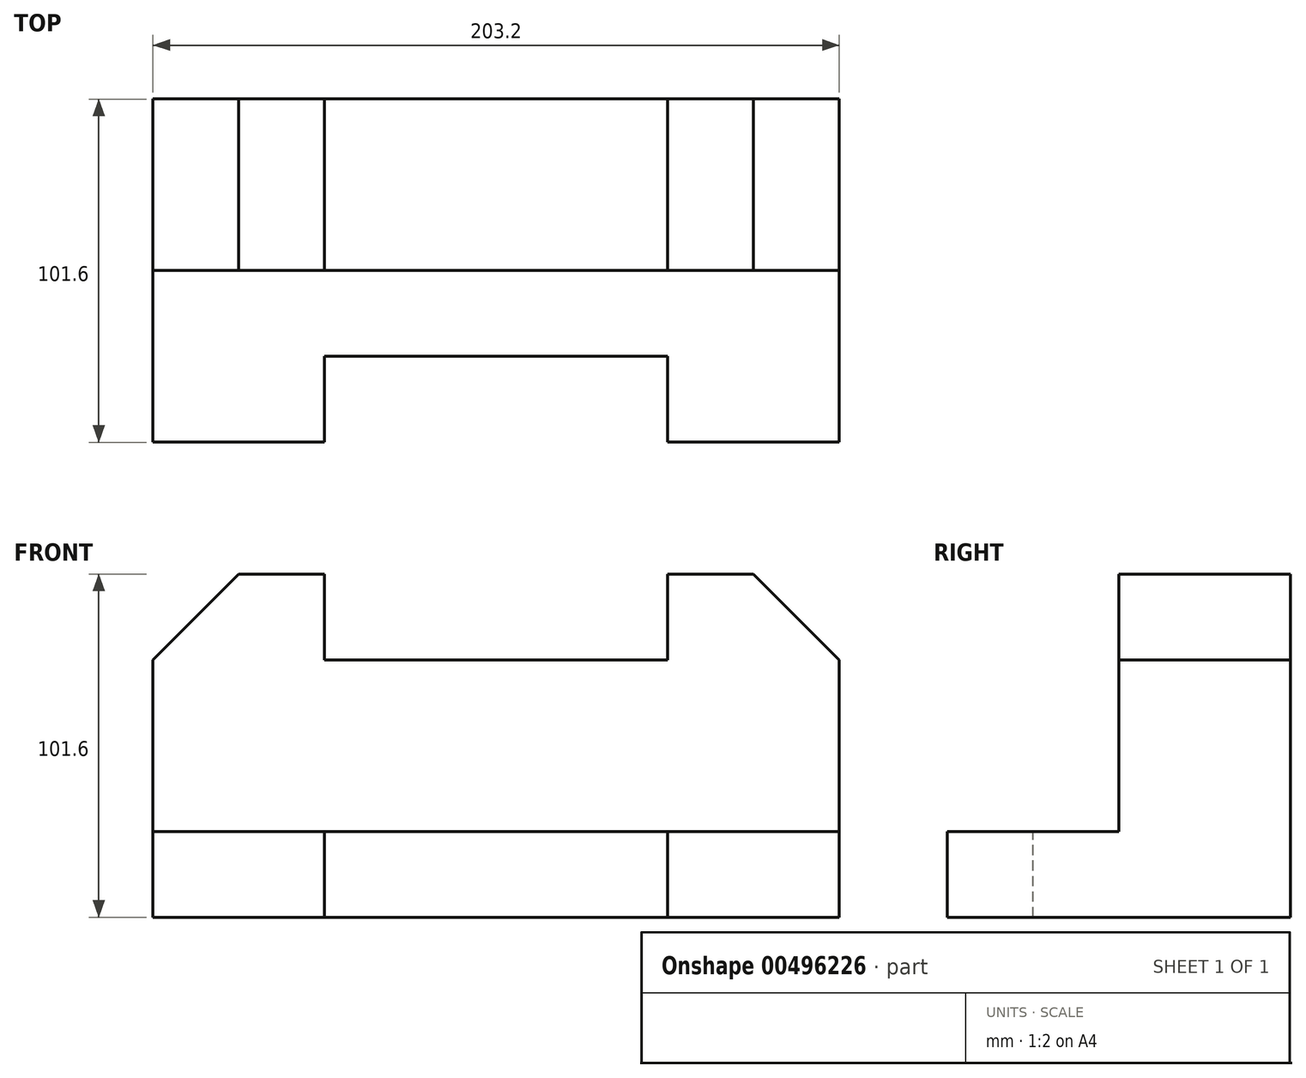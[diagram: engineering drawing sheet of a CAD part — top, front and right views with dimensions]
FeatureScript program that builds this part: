
annotation { "Feature Type Name" : "Feature", "Feature Type Description" : "" }
export const myFeature = defineFeature(function(context is Context, id is Id, definition is map)
    precondition{}
    {
        {
            var Q0;
            Q0=qCreatedBy(makeId("Top.planeOp"),FACE);
            var sketch = newSketch(context, id + "F0", { "sketchPlane" : qUnion([Q0])});
            skLineSegment(sketch, "E0.bottom", {"start": v(-130.96, 84.04) * mm, "end": v(72.24, 84.04) * mm});
            skLineSegment(sketch, "E0.top", {"start": v(-130.96, -17.56) * mm, "end": v(72.24, -17.56) * mm});
            skLineSegment(sketch, "E0.left", {"start": v(-130.96, 84.04) * mm, "end": v(-130.96, -17.56) * mm});
            skLineSegment(sketch, "E0.right", {"start": v(72.24, 84.04) * mm, "end": v(72.24, -17.56) * mm});
            skSolve(sketch);
        }
        {
            var Q0;
            Q0 = qSketchRegion(id + "F0", true);
            extrude(context, id + "F1", {"entities" : qUnion([Q0]), "depth" : 25.4 * mm});
        }
        {
            var Q0;
            Q0=makeQuery(id+"F1.opExtrude","CAP_FACE",FACE,{"disambiguationData":[OSD([sQuery(id+"F0.wireOp",EDGE,"E0.bottom"),sQuery(id+"F0.wireOp",EDGE,"E0.top"),sQuery(id+"F0.wireOp",EDGE,"E0.left"),sQuery(id+"F0.wireOp",EDGE,"E0.right")])],"isStart":false});
            var sketch = newSketch(context, id + "F2", { "sketchPlane" : qUnion([Q0])});
            skLineSegment(sketch, "E1.bottom", {"start": v(-130.96, 84.04) * mm, "end": v(72.24, 84.04) * mm});
            skLineSegment(sketch, "E1.top", {"start": v(-130.96, 33.24) * mm, "end": v(72.24, 33.24) * mm});
            skLineSegment(sketch, "E1.left", {"start": v(-130.96, 84.04) * mm, "end": v(-130.96, 33.24) * mm});
            skLineSegment(sketch, "E1.right", {"start": v(72.24, 84.04) * mm, "end": v(72.24, 33.24) * mm});
            skSolve(sketch);
        }
        {
            var Q0;
            Q0=makeQuery(id+"F2.imprint","IMPRINT",FACE,{"disambiguationData":[TD([[makeQuery(id+"F2.imprint","IMPRINT",EDGE,{"derivedFrom":sQuery(id+"F2.wireOp",EDGE,"E1.bottom")}),-1.0]])]});
            extrude(context, id + "F3", {"entities" : qUnion([Q0]), "operationType" : NewBodyOperationType.ADD, "depth" : 76.2 * mm});
        }
        {
            var Q0;
            Q0=makeQuery(id+"F1.opExtrude","CAP_FACE",FACE,{"disambiguationData":[OSD([sQuery(id+"F0.wireOp",EDGE,"E0.bottom"),sQuery(id+"F0.wireOp",EDGE,"E0.top"),sQuery(id+"F0.wireOp",EDGE,"E0.left"),sQuery(id+"F0.wireOp",EDGE,"E0.right")])],"isStart":false});
            var sketch = newSketch(context, id + "F4", { "sketchPlane" : qUnion([Q0])});
            skLineSegment(sketch, "E2.bottom", {"start": v(-80.16, -17.56) * mm, "end": v(21.44, -17.56) * mm});
            skLineSegment(sketch, "E2.top", {"start": v(-80.16, 7.84) * mm, "end": v(21.44, 7.84) * mm});
            skLineSegment(sketch, "E2.left", {"start": v(-80.16, -17.56) * mm, "end": v(-80.16, 7.84) * mm});
            skLineSegment(sketch, "E2.right", {"start": v(21.44, -17.56) * mm, "end": v(21.44, 7.84) * mm});
            skSolve(sketch);
        }
        {
            var Q0;
            Q0=makeQuery(id+"F4.imprint","IMPRINT",FACE,{"disambiguationData":[TD([[makeQuery(id+"F4.imprint","IMPRINT",EDGE,{"derivedFrom":sQuery(id+"F4.wireOp",EDGE,"E2.bottom")}),1.0]])]});
            extrude(context, id + "F5", {"entities" : qUnion([Q0]), "operationType" : NewBodyOperationType.REMOVE, "endBound" : BoundingType.UP_TO_NEXT, "oppositeDirection" : true, "depth" : 25.4 * mm});
        }
        {
            var Q0;
            Q0=makeQuery(id+"F3.opExtrude","SWEPT_FACE",FACE,{"disambiguationData":[OSD([sQuery(id+"F2.wireOp",EDGE,"E1.top")])]});
            var sketch = newSketch(context, id + "F6", { "sketchPlane" : qUnion([Q0])});
            skLineSegment(sketch, "E3.bottom", {"start": v(-80.16, 101.6) * mm, "end": v(21.44, 101.6) * mm});
            skLineSegment(sketch, "E3.top", {"start": v(-80.16, 76.2) * mm, "end": v(21.44, 76.2) * mm});
            skLineSegment(sketch, "E3.left", {"start": v(-80.16, 101.6) * mm, "end": v(-80.16, 76.2) * mm});
            skLineSegment(sketch, "E3.right", {"start": v(21.44, 101.6) * mm, "end": v(21.44, 76.2) * mm});
            skSolve(sketch);
        }
        {
            var Q0;
            Q0=makeQuery(id+"F6.imprint","IMPRINT",FACE,{"disambiguationData":[TD([[makeQuery(id+"F6.imprint","IMPRINT",EDGE,{"derivedFrom":sQuery(id+"F6.wireOp",EDGE,"E3.bottom")}),-1.0]])]});
            extrude(context, id + "F7", {"entities" : qUnion([Q0]), "operationType" : NewBodyOperationType.REMOVE, "endBound" : BoundingType.UP_TO_NEXT, "oppositeDirection" : true, "depth" : 25.4 * mm});
        }
        {
            var Q0;
            Q0=makeQuery(id+"F3.opExtrude","SWEPT_FACE",FACE,{"disambiguationData":[OSD([sQuery(id+"F2.wireOp",EDGE,"E1.top")])]});
            var sketch = newSketch(context, id + "F8", { "sketchPlane" : qUnion([Q0])});
            skLineSegment(sketch, "E4", {"start": v(-105.56, 101.6) * mm, "end": v(-130.96, 76.2) * mm});
            skLineSegment(sketch, "E5", {"start": v(-130.96, 76.2) * mm, "end": v(-130.96, 101.6) * mm});
            skLineSegment(sketch, "E6", {"start": v(-130.96, 101.6) * mm, "end": v(-105.56, 101.6) * mm});
            skLineSegment(sketch, "E7", {"start": v(46.84, 101.6) * mm, "end": v(72.24, 76.2) * mm});
            skLineSegment(sketch, "E8", {"start": v(72.24, 76.2) * mm, "end": v(72.24, 101.6) * mm});
            skLineSegment(sketch, "E9", {"start": v(72.24, 101.6) * mm, "end": v(46.84, 101.6) * mm});
            skSolve(sketch);
        }
        {
            var Q0;
            Q0 = qSketchRegion(id + "F8", true);
            extrude(context, id + "F9", {"entities" : qUnion([Q0]), "operationType" : NewBodyOperationType.REMOVE, "endBound" : BoundingType.UP_TO_NEXT, "oppositeDirection" : true, "depth" : 25.4 * mm});
        }
    });
